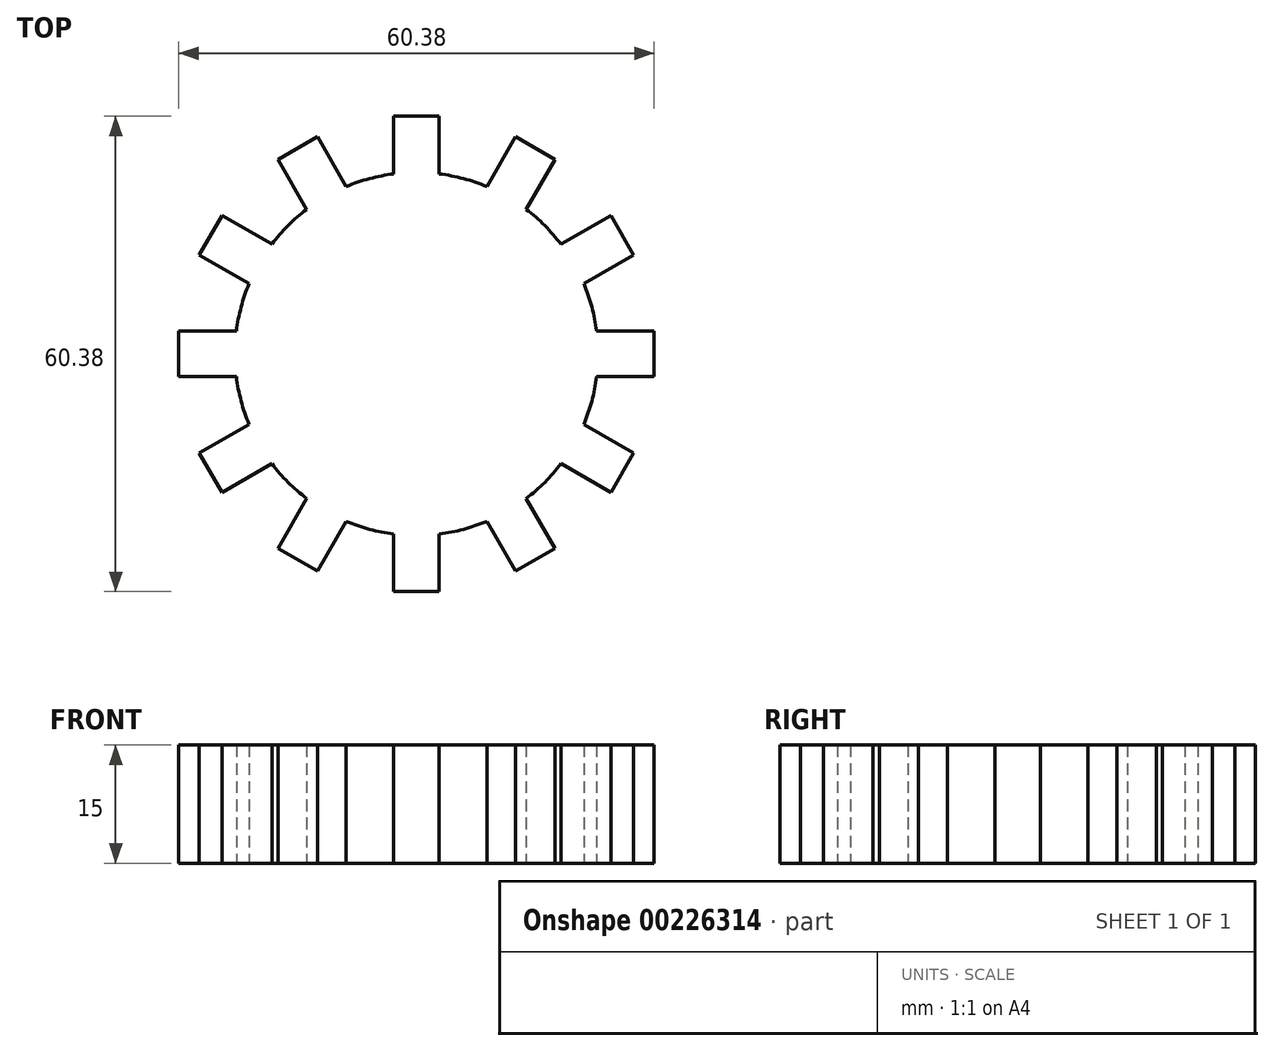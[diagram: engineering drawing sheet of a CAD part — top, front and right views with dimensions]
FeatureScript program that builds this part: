
annotation { "Feature Type Name" : "Feature", "Feature Type Description" : "" }
export const myFeature = defineFeature(function(context is Context, id is Id, definition is map)
    precondition{}
    {
        {
            var Q0;
            Q0=qCreatedBy(makeId("Top.planeOp"),FACE);
            var sketch = newSketch(context, id + "F0", { "sketchPlane" : qUnion([Q0])});
            skArc(sketch, "E0", {"start": v(-2.89, 22.88) * mm, "mid": v(-5.97, 22.27) * mm, "end": v(-8.94, 21.26) * mm});
            skLineSegment(sketch, "E1", {"start": v(-2.89, 22.88) * mm, "end": v(-2.89, 30.2) * mm});
            skLineSegment(sketch, "E2", {"start": v(-2.89, 30.2) * mm, "end": v(2.89, 30.2) * mm});
            skLineSegment(sketch, "E3", {"start": v(2.89, 30.2) * mm, "end": v(2.89, 22.88) * mm});
            skLineSegment(sketch, "E4.1.0", {"start": v(-13.94, 18.37) * mm, "end": v(-17.6, 24.7) * mm});
            skLineSegment(sketch, "E4.1.1", {"start": v(-17.6, 24.7) * mm, "end": v(-12.6, 27.6) * mm});
            skLineSegment(sketch, "E4.1.2", {"start": v(-12.6, 27.6) * mm, "end": v(-8.94, 21.26) * mm});
            skLineSegment(sketch, "E4.2.0", {"start": v(-21.26, 8.94) * mm, "end": v(-27.6, 12.6) * mm});
            skLineSegment(sketch, "E4.2.1", {"start": v(-27.6, 12.6) * mm, "end": v(-24.7, 17.6) * mm});
            skLineSegment(sketch, "E4.2.2", {"start": v(-24.7, 17.6) * mm, "end": v(-18.37, 13.94) * mm});
            skLineSegment(sketch, "E5.1.3.0", {"start": v(-22.88, -2.89) * mm, "end": v(-30.2, -2.89) * mm});
            skLineSegment(sketch, "E5.3.3.0", {"start": v(-30.2, -2.89) * mm, "end": v(-30.2, 2.89) * mm});
            skLineSegment(sketch, "E5.6.3.0", {"start": v(-30.2, 2.89) * mm, "end": v(-22.88, 2.89) * mm});
            skLineSegment(sketch, "E5.1.4.0", {"start": v(-18.37, -13.94) * mm, "end": v(-24.7, -17.6) * mm});
            skLineSegment(sketch, "E5.3.4.0", {"start": v(-24.7, -17.6) * mm, "end": v(-27.6, -12.6) * mm});
            skLineSegment(sketch, "E5.6.4.0", {"start": v(-27.6, -12.6) * mm, "end": v(-21.26, -8.94) * mm});
            skLineSegment(sketch, "E5.1.5.0", {"start": v(-8.94, -21.26) * mm, "end": v(-12.6, -27.6) * mm});
            skLineSegment(sketch, "E5.3.5.0", {"start": v(-12.6, -27.6) * mm, "end": v(-17.6, -24.7) * mm});
            skLineSegment(sketch, "E5.6.5.0", {"start": v(-17.6, -24.7) * mm, "end": v(-13.94, -18.37) * mm});
            skLineSegment(sketch, "E5.1.6.0", {"start": v(2.89, -22.88) * mm, "end": v(2.89, -30.2) * mm});
            skLineSegment(sketch, "E5.3.6.0", {"start": v(2.89, -30.2) * mm, "end": v(-2.89, -30.2) * mm});
            skLineSegment(sketch, "E5.6.6.0", {"start": v(-2.89, -30.2) * mm, "end": v(-2.89, -22.88) * mm});
            skLineSegment(sketch, "E5.1.7.0", {"start": v(13.94, -18.37) * mm, "end": v(17.6, -24.7) * mm});
            skLineSegment(sketch, "E5.3.7.0", {"start": v(17.6, -24.7) * mm, "end": v(12.6, -27.6) * mm});
            skLineSegment(sketch, "E5.6.7.0", {"start": v(12.6, -27.6) * mm, "end": v(8.94, -21.26) * mm});
            skLineSegment(sketch, "E5.1.8.0", {"start": v(21.26, -8.94) * mm, "end": v(27.6, -12.6) * mm});
            skLineSegment(sketch, "E5.3.8.0", {"start": v(27.6, -12.6) * mm, "end": v(24.7, -17.6) * mm});
            skLineSegment(sketch, "E5.6.8.0", {"start": v(24.7, -17.6) * mm, "end": v(18.37, -13.94) * mm});
            skLineSegment(sketch, "E5.1.9.0", {"start": v(22.88, 2.89) * mm, "end": v(30.2, 2.89) * mm});
            skLineSegment(sketch, "E5.3.9.0", {"start": v(30.2, 2.89) * mm, "end": v(30.2, -2.89) * mm});
            skLineSegment(sketch, "E5.6.9.0", {"start": v(30.2, -2.89) * mm, "end": v(22.88, -2.89) * mm});
            skLineSegment(sketch, "E5.1.10.0", {"start": v(18.37, 13.94) * mm, "end": v(24.7, 17.6) * mm});
            skLineSegment(sketch, "E5.3.10.0", {"start": v(24.7, 17.6) * mm, "end": v(27.6, 12.6) * mm});
            skLineSegment(sketch, "E5.6.10.0", {"start": v(27.6, 12.6) * mm, "end": v(21.26, 8.94) * mm});
            skLineSegment(sketch, "E5.1.11.0", {"start": v(8.94, 21.26) * mm, "end": v(12.6, 27.6) * mm});
            skLineSegment(sketch, "E5.3.11.0", {"start": v(12.6, 27.6) * mm, "end": v(17.6, 24.7) * mm});
            skLineSegment(sketch, "E5.6.11.0", {"start": v(17.6, 24.7) * mm, "end": v(13.94, 18.37) * mm});
            skArc(sketch, "E6.trimOffspring", {"start": v(8.94, 21.26) * mm, "mid": v(5.97, 22.27) * mm, "end": v(2.89, 22.88) * mm});
            skArc(sketch, "E7.trimOffspring", {"start": v(18.37, 13.94) * mm, "mid": v(16.3, 16.3) * mm, "end": v(13.94, 18.37) * mm});
            skArc(sketch, "E8.trimOffspring", {"start": v(22.88, 2.89) * mm, "mid": v(22.27, 5.97) * mm, "end": v(21.26, 8.94) * mm});
            skArc(sketch, "E9.trimOffspring", {"start": v(21.26, -8.94) * mm, "mid": v(22.27, -5.97) * mm, "end": v(22.88, -2.89) * mm});
            skArc(sketch, "E10.trimOffspring", {"start": v(13.94, -18.37) * mm, "mid": v(16.3, -16.3) * mm, "end": v(18.37, -13.94) * mm});
            skArc(sketch, "E11.trimOffspring", {"start": v(2.89, -22.88) * mm, "mid": v(5.97, -22.27) * mm, "end": v(8.94, -21.26) * mm});
            skArc(sketch, "E12.trimOffspring", {"start": v(-8.94, -21.26) * mm, "mid": v(-5.97, -22.27) * mm, "end": v(-2.89, -22.88) * mm});
            skArc(sketch, "E13.trimOffspring", {"start": v(-18.37, -13.94) * mm, "mid": v(-16.3, -16.3) * mm, "end": v(-13.94, -18.37) * mm});
            skArc(sketch, "E14.trimOffspring", {"start": v(-22.88, -2.89) * mm, "mid": v(-22.27, -5.97) * mm, "end": v(-21.26, -8.94) * mm});
            skArc(sketch, "E15.trimOffspring", {"start": v(-21.26, 8.94) * mm, "mid": v(-22.27, 5.97) * mm, "end": v(-22.88, 2.89) * mm});
            skArc(sketch, "E16.trimOffspring", {"start": v(-13.94, 18.37) * mm, "mid": v(-16.3, 16.3) * mm, "end": v(-18.37, 13.94) * mm});
            skSolve(sketch);
        }
        {
            var Q0;
            Q0=makeQuery(id+"F0.imprint","IMPRINT",FACE,{"disambiguationData":[TD([[makeQuery(id+"F0.imprint","IMPRINT",EDGE,{"derivedFrom":sQuery(id+"F0.wireOp",EDGE,"E0")}),1.0]])]});
            extrude(context, id + "F1", {"entities" : qUnion([Q0]), "depth" : 15 * mm});
        }
    });
